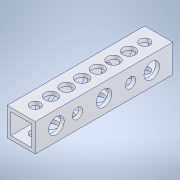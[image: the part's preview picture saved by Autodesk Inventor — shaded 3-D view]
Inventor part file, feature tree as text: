
AUTODESK INVENTOR PART (.ipt)
format: ipt  version: 2020.3 (Build 243373000, 373)  size: 202,240 bytes
history: native  units: mm
features: sketch x5, hole x4, other x1, extrude x1
ambient origin geometry x8: Origin, YZ Plane, XZ Plane, XY Plane, X Axis, Y Axis, Z Axis, Center Point
bodies: Body1 (feature_tree)
feature tree (11):
  other  "ソリッド1"
  extrude  "押し出し1"  Depth=9.0mm
  hole  "穴1"  [1 undecoded]
  hole  "穴2"  [1 undecoded]
  hole  "穴3"  [1 undecoded]
  hole  "穴4"  [1 undecoded]
  sketch  "スケッチ1"
  sketch  "スケッチ2"
  sketch  "スケッチ3"
  sketch  "スケッチ4"
  sketch  "スケッチ5"
note: 4 required parameter values undecoded (feature->parameter linkage not recoverable at this tier; creation-order binding heuristic only, values carry confidence <= 0.55)
